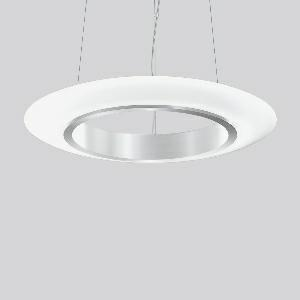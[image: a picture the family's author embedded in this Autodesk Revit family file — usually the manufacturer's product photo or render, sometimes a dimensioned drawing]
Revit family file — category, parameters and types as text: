
# Revit family: ring_of_fire_p_311570_004_730_e7ec
name_source: partatom
category: Lighting Fixtures
units: mm (PartAtom-declared; Revit-internal decimal feet)

## family parameters
Cut with Voids When Loaded = No
Host = Face
Light Source = No
Part Type = Normal
Room Calculation Point = No
Round Connector Dimension = Use Diameter
Shared = No

## types (1)
- RING OF FIRE P (1 x LED Modul 830, 4050 lm, 3000)
    Apparent Load = 37 VA
    CIE Flux Codes = 43 73 90 55 100
    Color Rendering = 80
    Color Temperature = 3000
    Default Elevation = 1800 mm
    Description = Series: RING OF FIRE
A uniquely shaped pendant luminaire with elliptical glass. Supporting ring made of anodised aluminium. Canopy aluminium anodised. Opal glass: mouth-blown, satin finish. Suitable for pendant. 3-point steel cable suspension, steplessly adjustable. Special lengths available on request. For pendant lengths of up to 2 m, power is supplied through a suspension cable. For pendant lengths of 2 m and more, power must be supplied through a separate cable. Converter integrated in the canopy. With Casambi smart+free Bluetooth control for wireless network and operation using Android / iOS devices, free app available for download. 
Colour: anodised aluminium
Diameter: 690 mm
Height: 81 mm
Suspension length: 500-1200 mm
Lamp: LED
Socket: without socket
Colour temperature: 3000K
Colour rendering index (CRI): 80
System power: 37 W
Rated luminous flux: 4050 lm
Luminous efficiency: 109 lm/W
Control gear: Dimmable Bluetooth converter
Protection class: I
Type of protection: IP 20
    Height = 81 mm
    Lamp = 1 x LED Modul 830
    Lamp Light Flux = 4050 lm
    Lamp count = 1
    Length = 690 mm
    Lifetime = 50000 h
    Luminous efficacy = 109 lm/W
    Manufacturer = RZB
    ModVariant = No
    Model = 311570.004.730
    Mounting Place = Ceiling
    Mounting Type = Pendant
    Number of Poles = 1
    OnlyDefault = Yes
    Power Factor = 1
    Product Name = RING OF FIRE P
    Product group = Pendant luminaires
    ProductGroupID = 902
    Protection Class = Protection class I
    Protection Degree = IP 20
    RLX_Detail_Level = 1
    RLX_Emergency_Light_Flux = 0 lm
    RLX_Emergency_Type = 0
    RLX_Emergency_Type_DB = No
    RlxData = <blob elided: 30661 chars, md5=20e6fc33>
    Socket = socket
    Standby Power = 0 W
    System Light Flux = 4050 lm
    System Power = 37 W
    Type Comments = Product without accessories
    Type Image = 311570.004.jpg
    URL = http://relux.com
    VarID = ---
    Voltage = 230 V
    Voltage Range = 220-240 V
    Weight = 0.00 kg
    Width = 0 mm  [stored 0 ft]

note: [stored X ft] marks values corroborated as IEEE doubles in the binary element streams (Revit-internal decimal feet)

## geometry (parser evidence)
native form markers: Blend x4, Sweep x12
no freeform markers — native parametric forms only
